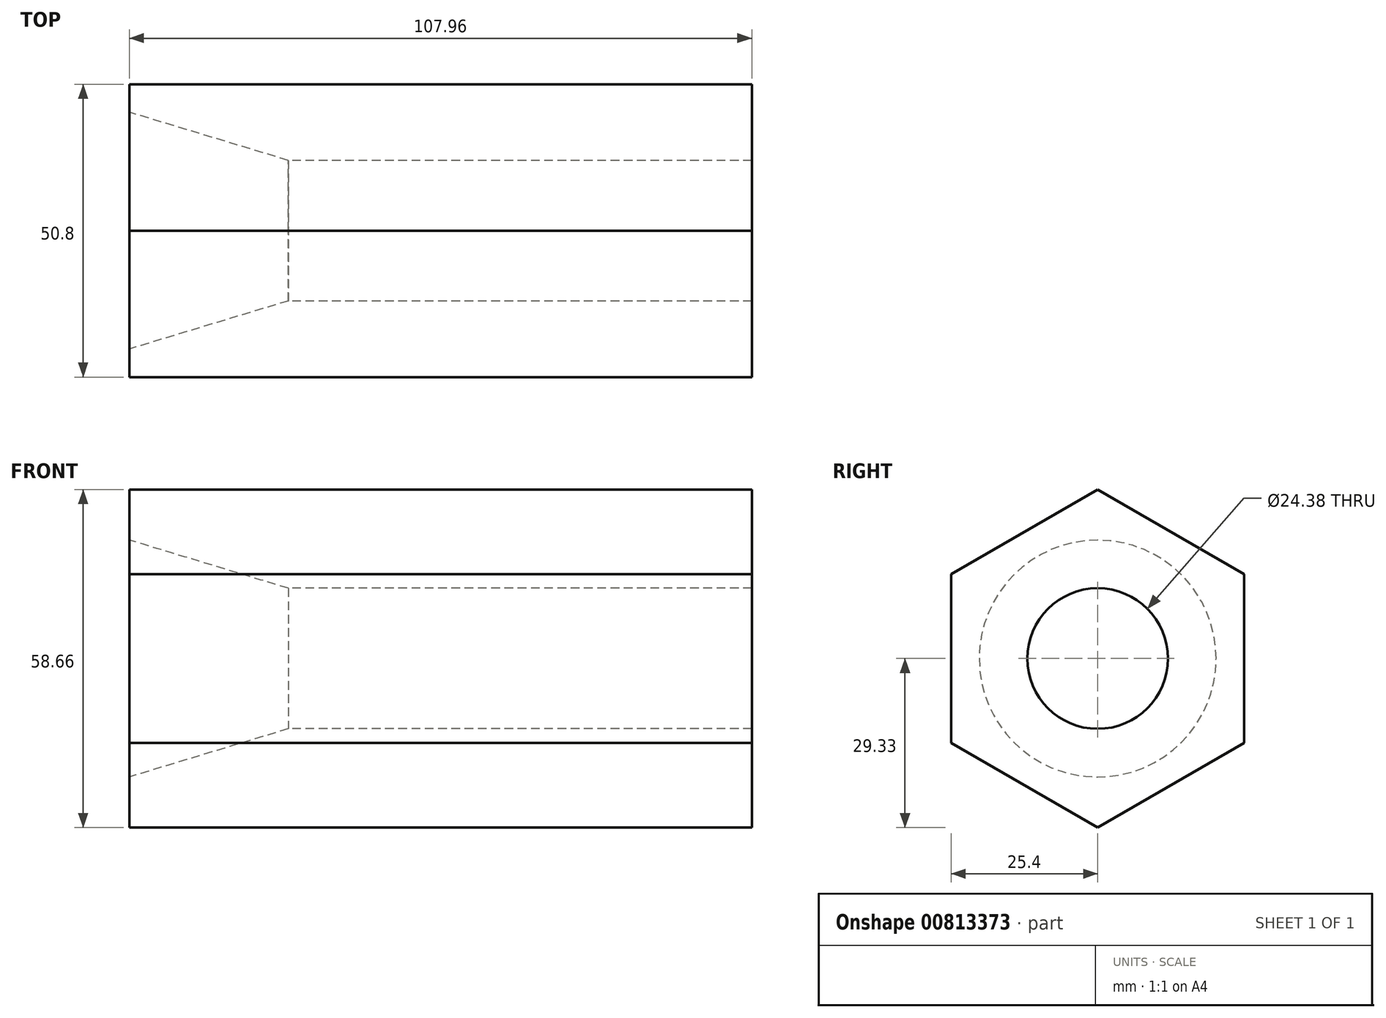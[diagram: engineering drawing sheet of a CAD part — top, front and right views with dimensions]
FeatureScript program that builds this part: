
annotation { "Feature Type Name" : "Feature", "Feature Type Description" : "" }
export const myFeature = defineFeature(function(context is Context, id is Id, definition is map)
    precondition{}
    {
        {
            var Q0;
            Q0=qCreatedBy(makeId("Right.planeOp"),FACE);
            var sketch = newSketch(context, id + "F0", { "sketchPlane" : qUnion([Q0])});
            skCircle(sketch, "E0.cCircle", {"center": v(0, 0) * mm, "radius": 25.4 * mm, "construction": true});
            skLineSegment(sketch, "E0.0", {"start": v(-25.4, -14.66) * mm, "end": v(-25.4, 14.66) * mm});
            skLineSegment(sketch, "E0.1", {"start": v(-25.4, 14.66) * mm, "end": v(0, 29.33) * mm});
            skLineSegment(sketch, "E0.2", {"start": v(0, 29.33) * mm, "end": v(25.4, 14.66) * mm});
            skLineSegment(sketch, "E0.3", {"start": v(25.4, 14.66) * mm, "end": v(25.4, -14.66) * mm});
            skLineSegment(sketch, "E0.4", {"start": v(25.4, -14.66) * mm, "end": v(0, -29.33) * mm});
            skLineSegment(sketch, "E0.5", {"start": v(0, -29.33) * mm, "end": v(-25.4, -14.66) * mm});
            skPoint(sketch, "E0.0.midPoint", {"position": v(-25.4, 0) * mm});
            skSolve(sketch);
        }
        {
            var Q0;
            Q0 = qSketchRegion(id + "F0", true);
            extrude(context, id + "F1", {"entities" : qUnion([Q0]), "endBound" : BoundingType.SYMMETRIC, "depth" : 107.95 * mm, "offsetDistance" : 25.4 * mm});
        }
        {
            var Q0;
            Q0=qCreatedBy(makeId("Front.planeOp"),FACE);
            var sketch = newSketch(context, id + "F2", { "sketchPlane" : qUnion([Q0])});
            skLineSegment(sketch, "E1", {"start": v(-76.68, 0) * mm, "end": v(75.97, 0) * mm, "construction": true});
            skLineSegment(sketch, "E2", {"start": v(53.98, 0) * mm, "end": v(53.98, 12.2) * mm});
            skLineSegment(sketch, "E3", {"start": v(53.98, 12.2) * mm, "end": v(-26.4, 12.2) * mm});
            skLineSegment(sketch, "E4", {"start": v(-26.4, 12.2) * mm, "end": v(-53.98, 20.54) * mm});
            skLineSegment(sketch, "E5", {"start": v(-53.98, 20.54) * mm, "end": v(-53.98, 0) * mm});
            skLineSegment(sketch, "E6", {"start": v(-53.98, 0) * mm, "end": v(53.98, 0) * mm});
            skSolve(sketch);
        }
        {
            var Q0;
            Q0 = qSketchRegion(id + "F2", true);
            var Q1;
            Q1=sQuery(id+"F2.wireOp",EDGE,"E1");
            revolve(context, id + "F3", {"operationType" : NewBodyOperationType.REMOVE, "surfaceOperationType" : NewSurfaceOperationType.NEW, "entities" : qUnion([Q0]), "axis" : qUnion([Q1]), "revolveType" : RevolveType.FULL});
        }
    });
